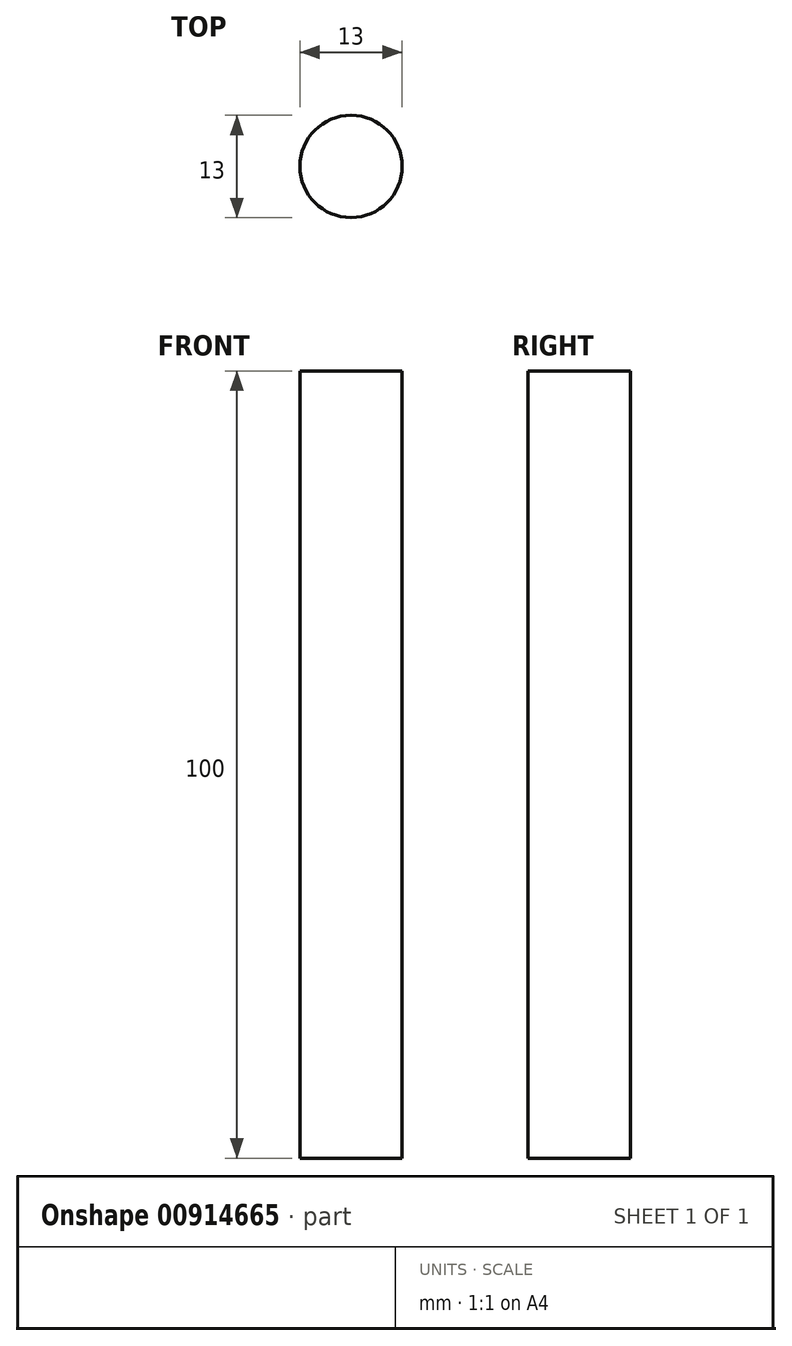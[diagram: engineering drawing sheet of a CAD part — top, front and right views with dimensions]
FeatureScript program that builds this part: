
annotation { "Feature Type Name" : "Feature", "Feature Type Description" : "" }
export const myFeature = defineFeature(function(context is Context, id is Id, definition is map)
    precondition{}
    {
        {
            var Q0;
            Q0=qCreatedBy(makeId("Top.planeOp"),FACE);
            var sketch = newSketch(context, id + "F0", { "sketchPlane" : qUnion([Q0])});
            skPoint(sketch, "E0", {"position": v(0, 0) * mm});
            skCircle(sketch, "E1", {"center": v(0, 0) * mm, "radius": 6.5 * mm});
            skSolve(sketch);
        }
        {
            var Q0;
            Q0=makeQuery(id+"F0.imprint","IMPRINT",FACE,{"disambiguationData":[TD([[makeQuery(id+"F0.imprint","IMPRINT",EDGE,{"derivedFrom":sQuery(id+"F0.wireOp",EDGE,"E1")}),1.0]])]});
            extrude(context, id + "F1", {"entities" : qUnion([Q0]), "depth" : 100 * mm, "offsetDistance" : 25 * mm});
        }
    });
